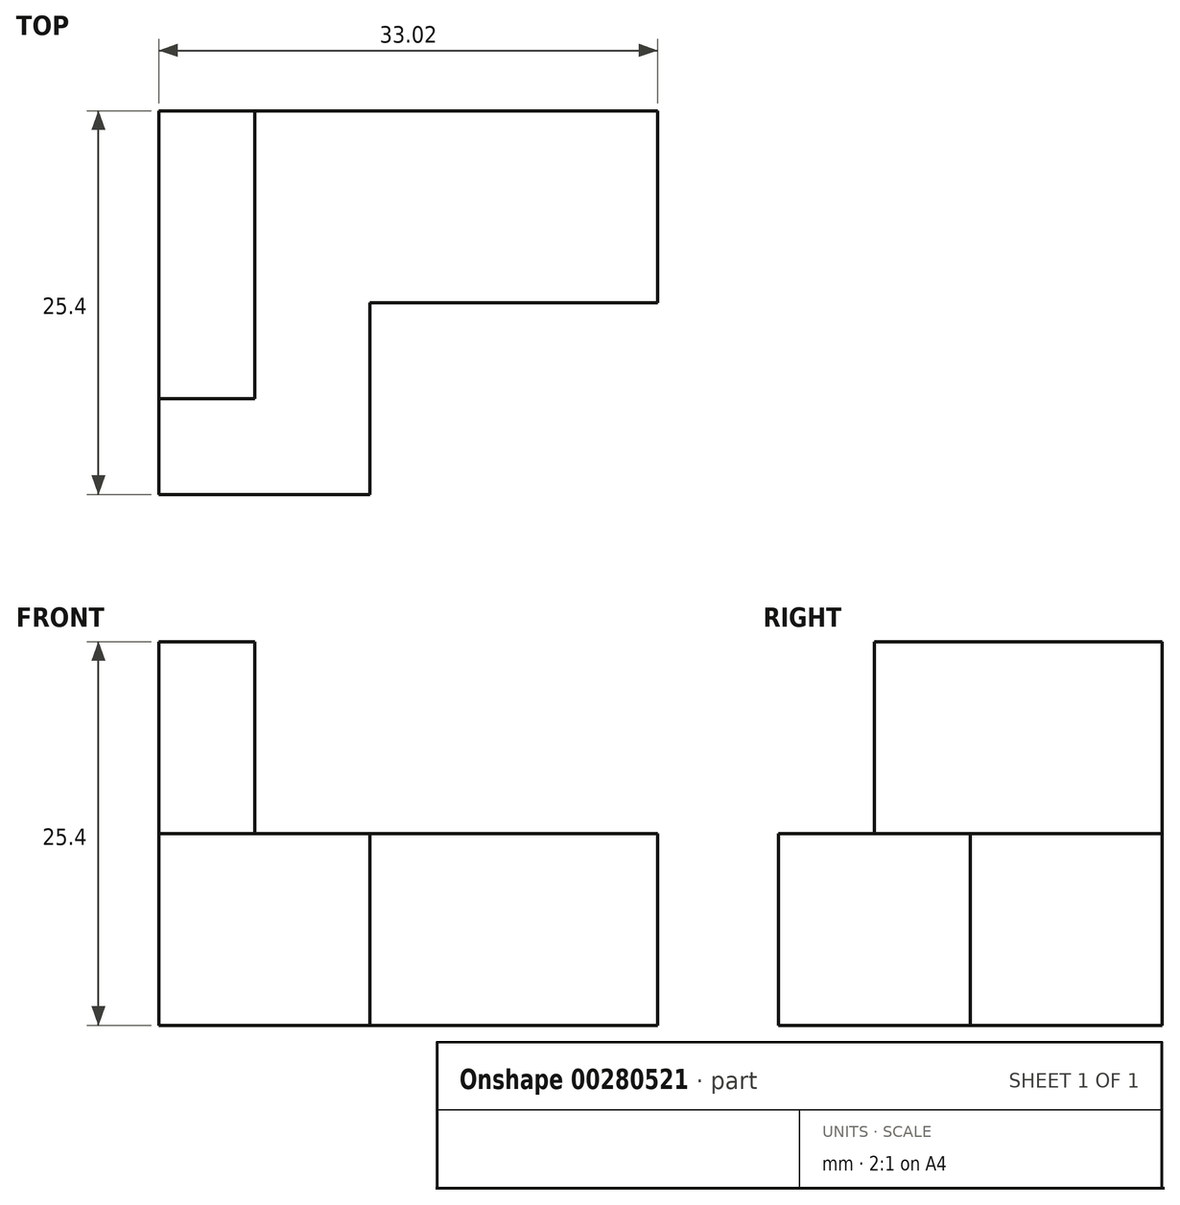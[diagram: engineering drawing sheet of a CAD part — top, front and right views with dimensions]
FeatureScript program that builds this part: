
annotation { "Feature Type Name" : "Feature", "Feature Type Description" : "" }
export const myFeature = defineFeature(function(context is Context, id is Id, definition is map)
    precondition{}
    {
        {
            var Q0;
            Q0=qCreatedBy(makeId("Front.planeOp"),FACE);
            var sketch = newSketch(context, id + "F0", { "sketchPlane" : qUnion([Q0])});
            skLineSegment(sketch, "E0", {"start": v(0, 0) * mm, "end": v(0, 25.4) * mm});
            skLineSegment(sketch, "E1", {"start": v(0, 25.4) * mm, "end": v(6.35, 25.4) * mm});
            skLineSegment(sketch, "E2", {"start": v(6.35, 25.4) * mm, "end": v(6.35, 12.7) * mm});
            skLineSegment(sketch, "E3", {"start": v(6.35, 12.7) * mm, "end": v(33.02, 12.7) * mm});
            skLineSegment(sketch, "E4", {"start": v(33.02, 12.7) * mm, "end": v(33.02, 0) * mm});
            skLineSegment(sketch, "E5", {"start": v(33.02, 0) * mm, "end": v(0, 0) * mm});
            skSolve(sketch);
        }
        {
            var Q0;
            Q0=makeQuery(id+"F0.imprint","IMPRINT",FACE,{"disambiguationData":[TD([[makeQuery(id+"F0.imprint","IMPRINT",EDGE,{"derivedFrom":sQuery(id+"F0.wireOp",EDGE,"E0")}),-1.0]])]});
            extrude(context, id + "F1", {"entities" : qUnion([Q0]), "depth" : 25.4 * mm});
        }
        {
            var Q0;
            Q0=makeQuery(id+"F1.opExtrude","CAP_FACE",FACE,{"disambiguationData":[OSD([sQuery(id+"F0.wireOp",EDGE,"E0"),sQuery(id+"F0.wireOp",EDGE,"E1"),sQuery(id+"F0.wireOp",EDGE,"E2"),sQuery(id+"F0.wireOp",EDGE,"E3"),sQuery(id+"F0.wireOp",EDGE,"E4"),sQuery(id+"F0.wireOp",EDGE,"E5")])],"isStart":false});
            var sketch = newSketch(context, id + "F2", { "sketchPlane" : qUnion([Q0])});
            skLineSegment(sketch, "E6", {"start": v(6.35, 12.7) * mm, "end": v(0, 12.7) * mm});
            skSolve(sketch);
        }
        {
            var Q0;
            {var subQ0=sQuery(id+"F2.wireOp",EDGE,"E6");Q0=makeQuery(id+"F2.imprint","IMPRINT",FACE,{"disambiguationData":[TD([[makeQuery(id+"F2.imprint","IMPRINT",EDGE,{"derivedFrom":subQ0}),-1.0]])]});}
            extrude(context, id + "F3", {"entities" : qUnion([Q0]), "operationType" : NewBodyOperationType.REMOVE, "oppositeDirection" : true, "depth" : 6.35 * mm});
        }
        {
            var Q0;
            Q0=makeQuery(id+"F3.boolean.opBoolean","MERGE",FACE,{"derivedFrom":[makeQuery(id+"F1.opExtrude","SWEPT_FACE",FACE,{"disambiguationData":[OSD([sQuery(id+"F0.wireOp",EDGE,"E3")])]}),makeQuery(id+"F3.opExtrude","SWEPT_FACE",FACE,{"disambiguationData":[OSD([sQuery(id+"F2.wireOp",EDGE,"E6")])]})]});
            var sketch = newSketch(context, id + "F4", { "sketchPlane" : qUnion([Q0])});
            skLineSegment(sketch, "E7.bottom", {"start": v(33.02, -25.4) * mm, "end": v(13.97, -25.4) * mm});
            skLineSegment(sketch, "E7.top", {"start": v(33.02, -12.7) * mm, "end": v(13.97, -12.7) * mm});
            skLineSegment(sketch, "E7.left", {"start": v(33.02, -25.4) * mm, "end": v(33.02, -12.7) * mm});
            skLineSegment(sketch, "E7.right", {"start": v(13.97, -25.4) * mm, "end": v(13.97, -12.7) * mm});
            skSolve(sketch);
        }
        {
            var Q0;
            Q0=makeQuery(id+"F4.imprint","IMPRINT",FACE,{"disambiguationData":[TD([[makeQuery(id+"F4.imprint","IMPRINT",EDGE,{"derivedFrom":sQuery(id+"F4.wireOp",EDGE,"E7.bottom")}),1.0]])]});
            extrude(context, id + "F5", {"entities" : qUnion([Q0]), "operationType" : NewBodyOperationType.REMOVE, "endBound" : BoundingType.THROUGH_ALL, "oppositeDirection" : true, "depth" : 25.4 * mm});
        }
    });
